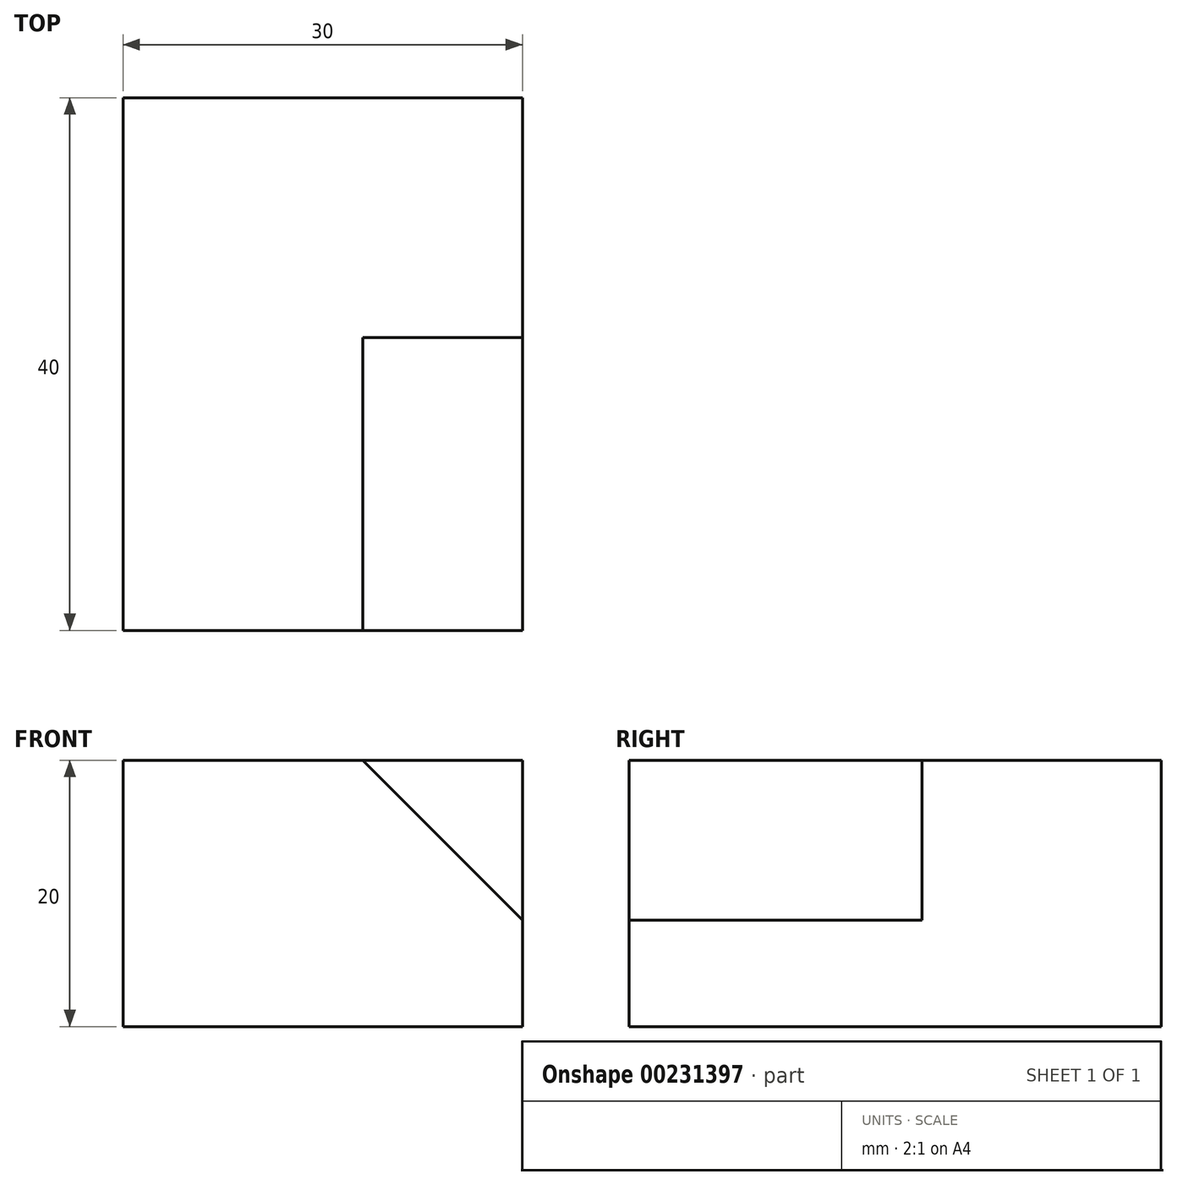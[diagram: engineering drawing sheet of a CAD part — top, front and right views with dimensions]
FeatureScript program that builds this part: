
annotation { "Feature Type Name" : "Feature", "Feature Type Description" : "" }
export const myFeature = defineFeature(function(context is Context, id is Id, definition is map)
    precondition{}
    {
        {
            var Q0;
            Q0=qCreatedBy(makeId("Front.planeOp"),FACE);
            var sketch = newSketch(context, id + "F0", { "sketchPlane" : qUnion([Q0])});
            skLineSegment(sketch, "E0.bottom", {"start": v(0, 0) * mm, "end": v(30, 0) * mm});
            skLineSegment(sketch, "E0.top", {"start": v(0, 20) * mm, "end": v(30, 20) * mm});
            skLineSegment(sketch, "E0.left", {"start": v(0, 0) * mm, "end": v(0, 20) * mm});
            skLineSegment(sketch, "E0.right", {"start": v(30, 0) * mm, "end": v(30, 20) * mm});
            skPoint(sketch, "E1", {"position": v(30, 20) * mm});
            skPoint(sketch, "E2", {"position": v(18, 20) * mm});
            skPoint(sketch, "E3", {"position": v(30, 8) * mm});
            skLineSegment(sketch, "E4", {"start": v(18, 20) * mm, "end": v(30, 8) * mm});
            skSolve(sketch);
        }
        {
            var Q0;
            {var subQ1=sQuery(id+"F0.wireOp",EDGE,"E0.bottom");Q0=makeQuery(id+"F0.imprint","IMPRINT",FACE,{"disambiguationData":[TD([[makeQuery(id+"F0.imprint","IMPRINT",EDGE,{"derivedFrom":subQ1}),1.0]])]});}
            var Q1;
            {var subQ3=sQuery(id+"F0.wireOp",EDGE,"E4");Q1=makeQuery(id+"F0.imprint","IMPRINT",FACE,{"disambiguationData":[TD([[makeQuery(id+"F0.imprint","IMPRINT",EDGE,{"derivedFrom":subQ3}),1.0]])]});}
            extrude(context, id + "F1", {"entities" : qUnion([Q0, Q1]), "oppositeDirection" : true, "depth" : 40 * mm});
        }
        {
            var Q0;
            Q0=qCreatedBy(makeId("Front.planeOp"),FACE);
            var sketch = newSketch(context, id + "F2", { "sketchPlane" : qUnion([Q0])});
            skLineSegment(sketch, "E5", {"start": v(18, 20) * mm, "end": v(30, 8) * mm});
            skLineSegment(sketch, "E6", {"start": v(18, 20) * mm, "end": v(30, 20) * mm});
            skLineSegment(sketch, "E7", {"start": v(30, 20) * mm, "end": v(30, 8) * mm});
            skSolve(sketch);
        }
        {
            var Q0;
            Q0=qSketchRegion(id+"F2",true);
            var Q1;
            Q1=makeQuery(id+"F1.opExtrude","CAP_FACE",FACE,{"disambiguationData":[OSD([sQuery(id+"F0.wireOp",EDGE,"E0.bottom"),sQuery(id+"F0.wireOp",EDGE,"E0.top"),sQuery(id+"F0.wireOp",EDGE,"E0.left"),sQuery(id+"F0.wireOp",EDGE,"E0.right")])],"isStart":false});
            extrude(context, id + "F3", {"entities" : qUnion([Q0, Q1]), "operationType" : NewBodyOperationType.REMOVE, "oppositeDirection" : true, "depth" : 22 * mm});
        }
    });
